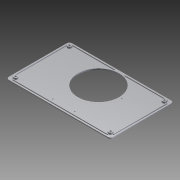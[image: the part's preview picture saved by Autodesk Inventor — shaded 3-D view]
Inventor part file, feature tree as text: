
AUTODESK INVENTOR PART (.ipt)
format: ipt  version: 2015 (Build 190159000, 159)  size: 189,440 bytes
history: native  units: in
note: dims shown in document units (in); Inventor stores cm internally (conversion verified against a paired STEP export)
features: reference x4, other x3, extrude x1, imported_body x1
ambient origin geometry x8: Origin, YZ Plane, XZ Plane, XY Plane, X Axis, Y Axis, Z Axis, Center Point
bodies: Body1 (feature_tree)
feature tree (9):
  other  "Lid"
  other  "Cut-Extrude3"
  other  "Lid.ipt1"
  extrude  "Extrusion2"  Depth=1.506in
  imported_body  "Base1"
  reference  "Reference2"
  reference  "Reference3"
  reference  "Reference4"
  reference  "Reference5"
